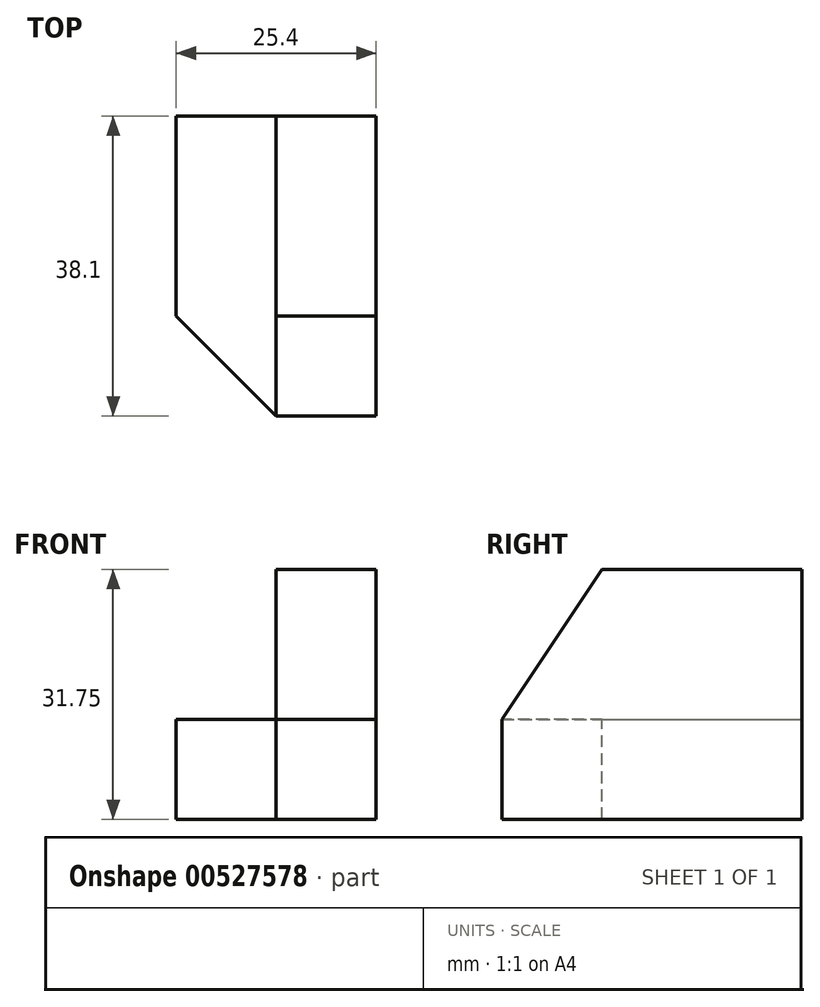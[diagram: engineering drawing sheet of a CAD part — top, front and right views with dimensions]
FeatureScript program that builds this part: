
annotation { "Feature Type Name" : "Feature", "Feature Type Description" : "" }
export const myFeature = defineFeature(function(context is Context, id is Id, definition is map)
    precondition{}
    {
        {
            var Q0;
            Q0=qCreatedBy(makeId("Front.planeOp"),FACE);
            var sketch = newSketch(context, id + "F0", { "sketchPlane" : qUnion([Q0])});
            skLineSegment(sketch, "E0", {"start": v(0, 0) * mm, "end": v(25.4, 0) * mm});
            skLineSegment(sketch, "E1", {"start": v(25.4, 0) * mm, "end": v(25.4, 31.75) * mm});
            skLineSegment(sketch, "E2", {"start": v(25.4, 31.75) * mm, "end": v(12.7, 31.75) * mm});
            skLineSegment(sketch, "E3", {"start": v(12.7, 31.75) * mm, "end": v(12.7, 12.7) * mm});
            skLineSegment(sketch, "E4", {"start": v(12.7, 12.7) * mm, "end": v(0, 12.7) * mm});
            skLineSegment(sketch, "E5", {"start": v(0, 12.7) * mm, "end": v(0, 0) * mm});
            skSolve(sketch);
        }
        {
            var Q0;
            Q0=makeQuery(id+"F0.imprint","IMPRINT",FACE,{"disambiguationData":[TD([[makeQuery(id+"F0.imprint","IMPRINT",EDGE,{"derivedFrom":sQuery(id+"F0.wireOp",EDGE,"E0")}),1.0]])]});
            extrude(context, id + "F1", {"entities" : qUnion([Q0]), "depth" : 38.1 * mm, "offsetDistance" : 25.4 * mm});
        }
        {
            var Q0;
            Q0=makeQuery(id+"F1.opExtrude","SWEPT_FACE",FACE,{"disambiguationData":[OSD([sQuery(id+"F0.wireOp",EDGE,"E4")])]});
            var sketch = newSketch(context, id + "F2", { "sketchPlane" : qUnion([Q0])});
            skLineSegment(sketch, "E6", {"start": v(0, 0) * mm, "end": v(0, -25.4) * mm});
            skLineSegment(sketch, "E7", {"start": v(0, -25.4) * mm, "end": v(12.7, -38.1) * mm});
            skSolve(sketch);
        }
        {
            var Q0;
            {var subQ0=sQuery(id+"F2.wireOp",EDGE,"E7");Q0=makeQuery(id+"F2.imprint","IMPRINT",FACE,{"disambiguationData":[TD([[makeQuery(id+"F2.imprint","IMPRINT",EDGE,{"derivedFrom":subQ0}),-1.0]])]});}
            extrude(context, id + "F3", {"entities" : qUnion([Q0]), "operationType" : NewBodyOperationType.REMOVE, "oppositeDirection" : true, "depth" : 12.7 * mm, "offsetDistance" : 25.4 * mm});
        }
        {
            var Q0;
            Q0=makeQuery(id+"F1.opExtrude","SWEPT_FACE",FACE,{"disambiguationData":[OSD([sQuery(id+"F0.wireOp",EDGE,"E3")])]});
            var sketch = newSketch(context, id + "F4", { "sketchPlane" : qUnion([Q0])});
            skLineSegment(sketch, "E8", {"start": v(0, 31.75) * mm, "end": v(25.4, 31.75) * mm});
            skLineSegment(sketch, "E9", {"start": v(25.4, 31.75) * mm, "end": v(38.1, 12.7) * mm});
            skSolve(sketch);
        }
        {
            var Q0;
            {var subQ0=sQuery(id+"F4.wireOp",EDGE,"E9");Q0=makeQuery(id+"F4.imprint","IMPRINT",FACE,{"disambiguationData":[TD([[makeQuery(id+"F4.imprint","IMPRINT",EDGE,{"derivedFrom":subQ0}),1.0]])]});}
            extrude(context, id + "F5", {"entities" : qUnion([Q0]), "operationType" : NewBodyOperationType.REMOVE, "oppositeDirection" : true, "depth" : 25.4 * mm, "offsetDistance" : 25.4 * mm});
        }
    });
